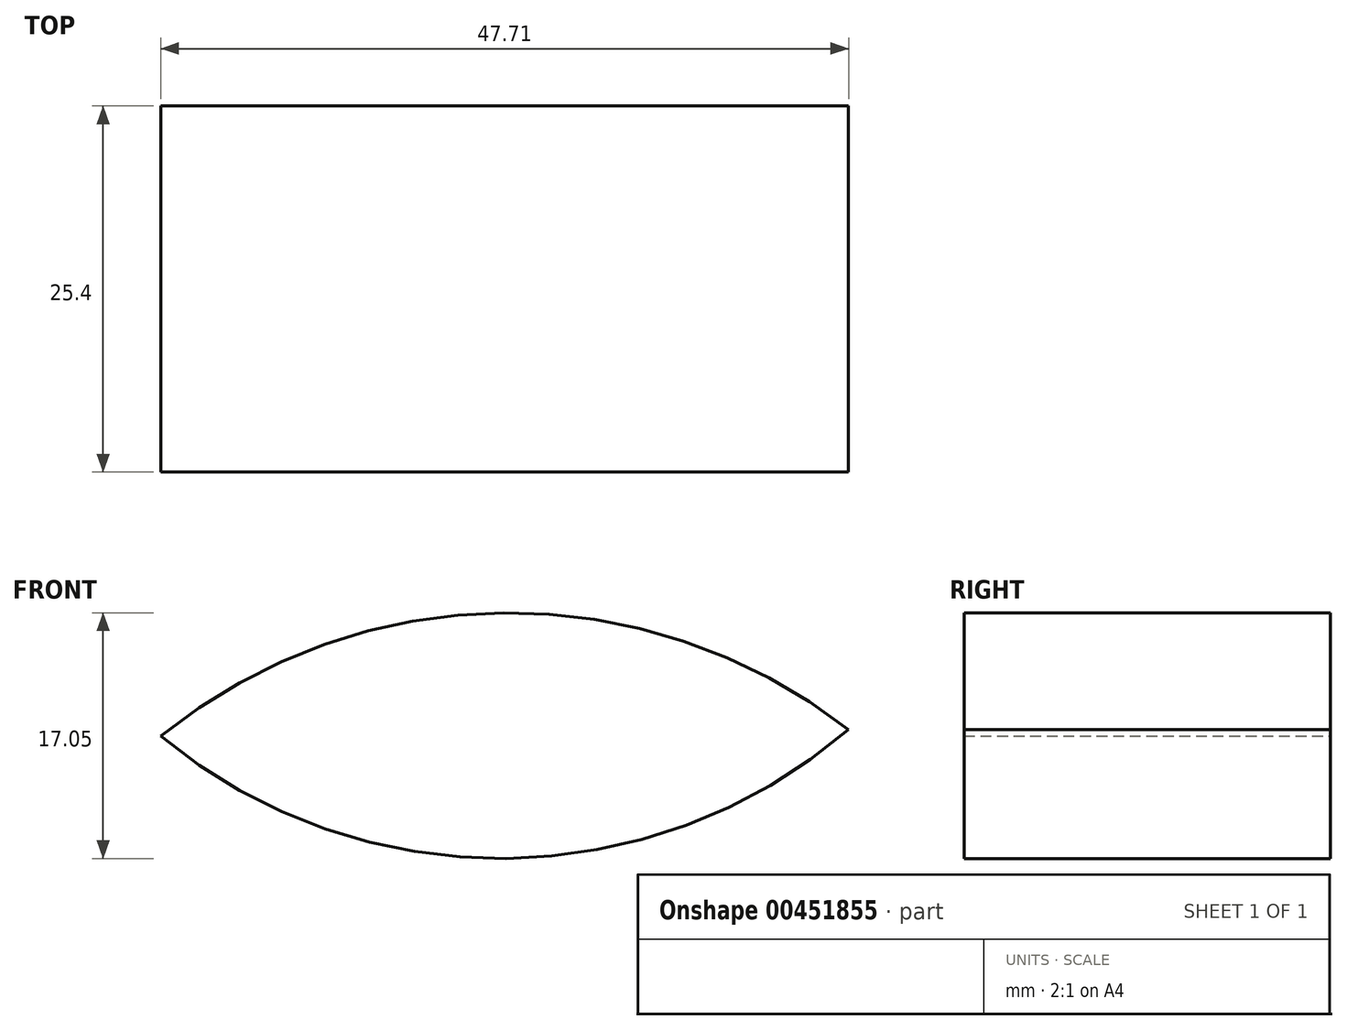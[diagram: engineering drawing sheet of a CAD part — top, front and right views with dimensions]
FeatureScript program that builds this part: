
annotation { "Feature Type Name" : "Feature", "Feature Type Description" : "" }
export const myFeature = defineFeature(function(context is Context, id is Id, definition is map)
    precondition{}
    {
        {
            var Q0;
            Q0=qCreatedBy(makeId("Front.planeOp"),FACE);
            var sketch = newSketch(context, id + "F0", { "sketchPlane" : qUnion([Q0])});
            skArc(sketch, "E0", {"start": v(-25.86, -33) * mm, "mid": v(-1.92, -41.48) * mm, "end": v(21.85, -32.55) * mm});
            skArc(sketch, "E1", {"start": v(21.85, -32.55) * mm, "mid": v(-2.08, -24.43) * mm, "end": v(-25.86, -33) * mm});
            skLineSegment(sketch, "E2", {"start": v(-25.86, -33) * mm, "end": v(-25.86, 45.03) * mm});
            skLineSegment(sketch, "E3", {"start": v(21.85, -32.55) * mm, "end": v(21.85, 45.03) * mm});
            skArc(sketch, "E4", {"start": v(-25.86, 45.03) * mm, "mid": v(-2, 38.2) * mm, "end": v(21.85, 45.03) * mm});
            skArc(sketch, "E5", {"start": v(-6.16, 53.15) * mm, "mid": v(-17.25, 52.1) * mm, "end": v(-25.86, 45.03) * mm});
            skLineSegment(sketch, "E6", {"start": v(-6.16, 53.15) * mm, "end": v(-6.16, 62.97) * mm});
            skArc(sketch, "E7", {"start": v(21.85, 45.03) * mm, "mid": v(14.4, 51.02) * mm, "end": v(5, 52.73) * mm});
            skLineSegment(sketch, "E8", {"start": v(5, 52.73) * mm, "end": v(5, 63.44) * mm});
            skLineSegment(sketch, "E9", {"start": v(-6.16, 62.97) * mm, "end": v(-24.03, 59.8) * mm});
            skArc(sketch, "E10", {"start": v(-24.03, 59.8) * mm, "mid": v(-29.3, 56.87) * mm, "end": v(-31.63, 51.31) * mm});
            skLineSegment(sketch, "E11", {"start": v(-31.63, 51.31) * mm, "end": v(-39.22, 65.57) * mm});
            skLineSegment(sketch, "E12", {"start": v(-39.22, 65.57) * mm, "end": v(-5.71, 71.9) * mm});
            skLineSegment(sketch, "E13", {"start": v(-5.71, 71.9) * mm, "end": v(-31.63, 81.2) * mm});
            skArc(sketch, "E14", {"start": v(-31.63, 81.2) * mm, "mid": v(-37.19, 81.18) * mm, "end": v(-41.45, 77.61) * mm});
            skLineSegment(sketch, "E15", {"start": v(-41.45, 77.61) * mm, "end": v(-41.45, 90.11) * mm});
            skArc(sketch, "E16", {"start": v(-41.45, 90.11) * mm, "mid": v(-38.48, 94.81) * mm, "end": v(-32.95, 94.14) * mm});
            skLineSegment(sketch, "E17", {"start": v(-32.95, 94.14) * mm, "end": v(-2, 83.28) * mm});
            skSolve(sketch);
        }
        {
            var Q0;
            Q0=makeQuery(id+"F0.imprint","IMPRINT",FACE,{"disambiguationData":[TD([[makeQuery(id+"F0.imprint","IMPRINT",EDGE,{"derivedFrom":sQuery(id+"F0.wireOp",EDGE,"E0")}),1.0]])]});
            extrude(context, id + "F1", {"entities" : qUnion([Q0]), "depth" : 25.4 * mm});
        }
    });
